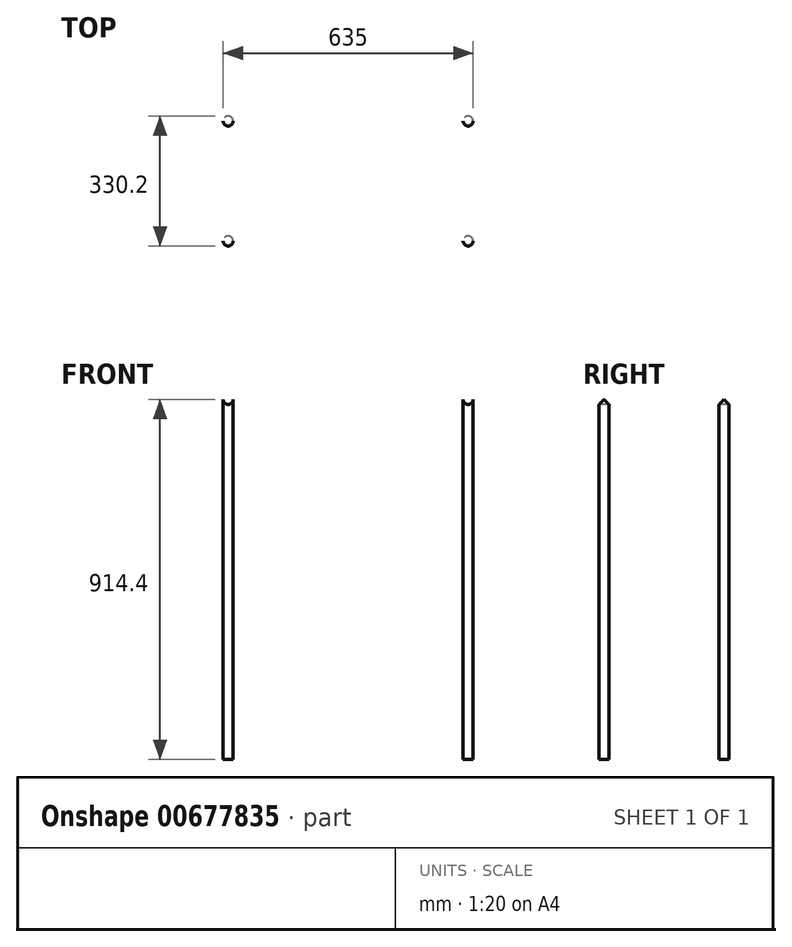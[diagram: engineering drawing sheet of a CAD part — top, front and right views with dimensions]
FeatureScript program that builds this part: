
annotation { "Feature Type Name" : "Feature", "Feature Type Description" : "" }
export const myFeature = defineFeature(function(context is Context, id is Id, definition is map)
    precondition{}
    {
        {
            var Q0;
            Q0=qCreatedBy(makeId("Top.planeOp"),FACE);
            var sketch = newSketch(context, id + "F0", { "sketchPlane" : qUnion([Q0])});
            skCircle(sketch, "E0", {"center": v(0, 0) * mm, "radius": 12.7 * mm});
            skCircle(sketch, "E1.0.1.0", {"center": v(0, 304.8) * mm, "radius": 12.7 * mm});
            skCircle(sketch, "E1.1.0.0", {"center": v(609.6, 0) * mm, "radius": 12.7 * mm});
            skCircle(sketch, "E1.1.1.0", {"center": v(609.6, 304.8) * mm, "radius": 12.7 * mm});
            skLineSegment(sketch, "E1.direction1", {"start": v(0, 0) * mm, "end": v(609.6, 0) * mm, "construction": true});
            skLineSegment(sketch, "E1.direction2", {"start": v(0, 0) * mm, "end": v(0, 304.8) * mm, "construction": true});
            skSolve(sketch);
        }
        {
            var Q0;
            Q0=makeQuery(id+"F0.imprint","IMPRINT",FACE,{"disambiguationData":[TD([[makeQuery(id+"F0.imprint","IMPRINT",EDGE,{"derivedFrom":sQuery(id+"F0.wireOp",EDGE,"E1.0.1.0")}),1.0]])]});
            var Q1;
            Q1=makeQuery(id+"F0.imprint","IMPRINT",FACE,{"disambiguationData":[TD([[makeQuery(id+"F0.imprint","IMPRINT",EDGE,{"derivedFrom":sQuery(id+"F0.wireOp",EDGE,"E0")}),1.0]])]});
            var Q2;
            Q2=makeQuery(id+"F0.imprint","IMPRINT",FACE,{"disambiguationData":[TD([[makeQuery(id+"F0.imprint","IMPRINT",EDGE,{"derivedFrom":sQuery(id+"F0.wireOp",EDGE,"E1.1.1.0")}),1.0]])]});
            var Q3;
            Q3=makeQuery(id+"F0.imprint","IMPRINT",FACE,{"disambiguationData":[TD([[makeQuery(id+"F0.imprint","IMPRINT",EDGE,{"derivedFrom":sQuery(id+"F0.wireOp",EDGE,"E1.1.0.0")}),1.0]])]});
            extrude(context, id + "F1", {"entities" : qUnion([Q0, Q1, Q2, Q3]), "depth" : 914.4 * mm, "offsetDistance" : 25.4 * mm});
        }
        {
            var Q0;
            Q0=qCreatedBy(makeId("Front.planeOp"),FACE);
            var sketch = newSketch(context, id + "F2", { "sketchPlane" : qUnion([Q0])});
            skCircle(sketch, "E2", {"center": v(0, 914.4) * mm, "radius": 12.7 * mm});
            skCircle(sketch, "E3.1.0.0", {"center": v(609.6, 914.4) * mm, "radius": 12.7 * mm});
            skLineSegment(sketch, "E3.direction1", {"start": v(0, 914.4) * mm, "end": v(609.6, 914.4) * mm, "construction": true});
            skSolve(sketch);
        }
        {
            var Q0;
            Q0=makeQuery(id+"F2.imprint","IMPRINT",FACE,{"disambiguationData":[TD([[makeQuery(id+"F2.imprint","IMPRINT",EDGE,{"derivedFrom":sQuery(id+"F2.wireOp",EDGE,"E2")}),1.0]])]});
            var Q1;
            Q1=makeQuery(id+"F2.imprint","IMPRINT",FACE,{"disambiguationData":[TD([[makeQuery(id+"F2.imprint","IMPRINT",EDGE,{"derivedFrom":sQuery(id+"F2.wireOp",EDGE,"E3.1.0.0")}),1.0]])]});
            extrude(context, id + "F3", {"entities" : qUnion([Q0, Q1]), "operationType" : NewBodyOperationType.REMOVE, "endBound" : BoundingType.THROUGH_ALL, "oppositeDirection" : true, "depth" : 25.4 * mm, "offsetDistance" : 25.4 * mm, "hasSecondDirection" : true, "secondDirectionBound" : SecondDirectionBoundingType.THROUGH_ALL, "secondDirectionOppositeDirection" : false, "secondDirectionDepth" : 25.4 * mm});
        }
    });
